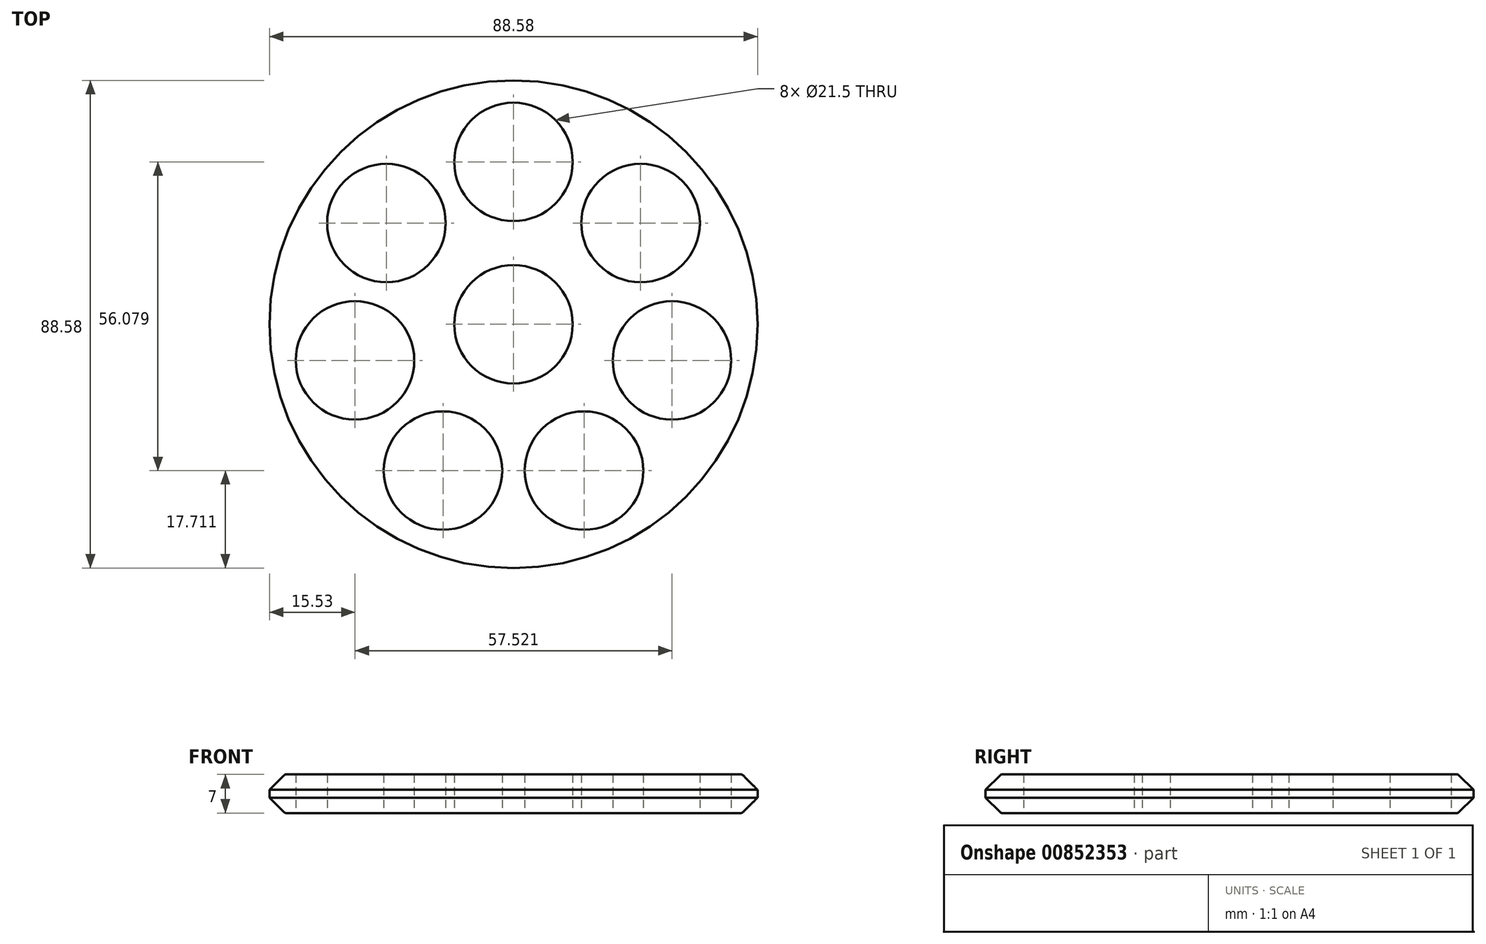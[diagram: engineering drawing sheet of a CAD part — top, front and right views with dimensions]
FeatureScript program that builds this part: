
annotation { "Feature Type Name" : "Feature", "Feature Type Description" : "" }
export const myFeature = defineFeature(function(context is Context, id is Id, definition is map)
    precondition{}
    {
        {
            var Q0;
            Q0=qCreatedBy(makeId("Top.planeOp"),FACE);
            var sketch = newSketch(context, id + "F0", { "sketchPlane" : qUnion([Q0])});
            skCircle(sketch, "E0", {"center": v(0, 0) * mm, "radius": 10.75 * mm});
            skCircle(sketch, "E1", {"center": v(0, 0) * mm, "radius": 45 * mm});
            skCircle(sketch, "E2", {"center": v(0, 29.5) * mm, "radius": 10.75 * mm});
            skCircle(sketch, "E3.1.0", {"center": v(-23.06, 18.4) * mm, "radius": 10.75 * mm});
            skCircle(sketch, "E3.2.0", {"center": v(-28.76, -6.56) * mm, "radius": 10.75 * mm});
            skCircle(sketch, "E3.3.0", {"center": v(-12.8, -26.58) * mm, "radius": 10.75 * mm});
            skCircle(sketch, "E3.4.0", {"center": v(12.8, -26.58) * mm, "radius": 10.75 * mm});
            skCircle(sketch, "E3.5.0", {"center": v(28.76, -6.56) * mm, "radius": 10.75 * mm});
            skCircle(sketch, "E3.6.0", {"center": v(23.06, 18.4) * mm, "radius": 10.75 * mm});
            skSolve(sketch);
        }
        {
            var Q0;
            Q0=makeQuery(id+"F0.imprint","IMPRINT",FACE,{"disambiguationData":[TD([[makeQuery(id+"F0.imprint","IMPRINT",EDGE,{"derivedFrom":sQuery(id+"F0.wireOp",EDGE,"E0")}),-1.0]])]});
            extrude(context, id + "F1", {"entities" : qUnion([Q0]), "depth" : 7 * mm, "offsetDistance" : 25 * mm});
        }
        {
            var Q0;
            Q0=makeQuery(id+"F1.opExtrude","CAP_EDGE",EDGE,{"disambiguationData":[OSD([sQuery(id+"F0.wireOp",EDGE,"E1")])],"isStart":false});
            var Q1;
            Q1=makeQuery(id+"F1.opExtrude","CAP_EDGE",EDGE,{"disambiguationData":[OSD([sQuery(id+"F0.wireOp",EDGE,"E1")])],"isStart":true});
            chamfer(context, id + "F2", {"entities" : qUnion([Q0, Q1]), "width" : 3.5 * mm, "tangentPropagation" : true});
        }
        {
            var Q0;
            {var subQ0=sQuery(id+"F0.wireOp",EDGE,"E1");Q0=makeQuery(id+"F2.opChamfer","BLEND_EDGE",EDGE,{"blendedFrom":[makeQuery(id+"F1.opExtrude","CAP_EDGE",EDGE,{"disambiguationData":[OSD([subQ0])],"isStart":false}),makeQuery(id+"F1.opExtrude","CAP_FACE",FACE,{"disambiguationData":[OSD([sQuery(id+"F0.wireOp",EDGE,"E0"),subQ0,sQuery(id+"F0.wireOp",EDGE,"E2"),sQuery(id+"F0.wireOp",EDGE,"E3.1.0"),sQuery(id+"F0.wireOp",EDGE,"E3.2.0"),sQuery(id+"F0.wireOp",EDGE,"E3.3.0"),sQuery(id+"F0.wireOp",EDGE,"E3.4.0"),sQuery(id+"F0.wireOp",EDGE,"E3.5.0"),sQuery(id+"F0.wireOp",EDGE,"E3.6.0")])],"isStart":false})],"blendedInto":[makeQuery(id+"F1.opExtrude","CAP_FACE",FACE,{"disambiguationData":[OSD([sQuery(id+"F0.wireOp",EDGE,"E0"),subQ0,sQuery(id+"F0.wireOp",EDGE,"E2"),sQuery(id+"F0.wireOp",EDGE,"E3.1.0"),sQuery(id+"F0.wireOp",EDGE,"E3.2.0"),sQuery(id+"F0.wireOp",EDGE,"E3.3.0"),sQuery(id+"F0.wireOp",EDGE,"E3.4.0"),sQuery(id+"F0.wireOp",EDGE,"E3.5.0"),sQuery(id+"F0.wireOp",EDGE,"E3.6.0")])],"isStart":false})]});}
            var Q1;
            {var subQ0=sQuery(id+"F0.wireOp",EDGE,"E1");Q1=makeQuery(id+"F2.opChamfer","BLEND_EDGE",EDGE,{"blendedFrom":[makeQuery(id+"F1.opExtrude","CAP_EDGE",EDGE,{"disambiguationData":[OSD([subQ0])],"isStart":true}),makeQuery(id+"F1.opExtrude","CAP_FACE",FACE,{"disambiguationData":[OSD([sQuery(id+"F0.wireOp",EDGE,"E0"),subQ0,sQuery(id+"F0.wireOp",EDGE,"E2"),sQuery(id+"F0.wireOp",EDGE,"E3.1.0"),sQuery(id+"F0.wireOp",EDGE,"E3.2.0"),sQuery(id+"F0.wireOp",EDGE,"E3.3.0"),sQuery(id+"F0.wireOp",EDGE,"E3.4.0"),sQuery(id+"F0.wireOp",EDGE,"E3.5.0"),sQuery(id+"F0.wireOp",EDGE,"E3.6.0")])],"isStart":true})],"blendedInto":[makeQuery(id+"F1.opExtrude","CAP_FACE",FACE,{"disambiguationData":[OSD([sQuery(id+"F0.wireOp",EDGE,"E0"),subQ0,sQuery(id+"F0.wireOp",EDGE,"E2"),sQuery(id+"F0.wireOp",EDGE,"E3.1.0"),sQuery(id+"F0.wireOp",EDGE,"E3.2.0"),sQuery(id+"F0.wireOp",EDGE,"E3.3.0"),sQuery(id+"F0.wireOp",EDGE,"E3.4.0"),sQuery(id+"F0.wireOp",EDGE,"E3.5.0"),sQuery(id+"F0.wireOp",EDGE,"E3.6.0")])],"isStart":true})]});}
            fillet(context, id + "F3", {"entities" : qUnion([Q0, Q1]), "radius" : .5 * mm, "tangentPropagation" : true, "allowEdgeOverflow" : false});
        }
        {
            var Q0;
            {var subQ0=sQuery(id+"F0.wireOp",EDGE,"E1");Q0=makeQuery(id+"F2.opChamfer","BLEND_EDGE",EDGE,{"blendedFrom":[makeQuery(id+"F1.opExtrude","CAP_EDGE",EDGE,{"disambiguationData":[OSD([subQ0])],"isStart":true}),makeQuery(id+"F1.opExtrude","CAP_EDGE",EDGE,{"disambiguationData":[OSD([subQ0])],"isStart":false})],"blendedInto":[]});}
            chamfer(context, id + "F4", {"entities" : qUnion([Q0]), "width" : 1 * mm, "tangentPropagation" : true});
        }
    });
